# Revit family: Cabinet_Wenger_UltraStor_35
name_source: partatom
category: Furniture
revit_build: Autodesk Revit 2015 (Build: 20140606_1530(x64)
units: mm (PartAtom-declared; Revit-internal decimal feet)

## types (4) — shared parameters
Assembly Code = E2010200
Cabinet Height = 7' - 1 5/8"
Cabinet Panel Thickness = 0' - 0 3/4"
Cabinet Width = 4' - 0 1/2"
Construction Details = http://www.arcat.com
Door Height = 6' - 8 7/8"
Door Width = 1' - 11 1/2"
Green Building-LEED = http://www.arcat.com
Installed Depth = 2' - 5 1/4"
Keynote = 12 35 83
Manufacturer = Wenger Corporation
Manufacturer Fax = (507) 455-4258
Manufacturer Website = https://www.wengercorp.com
Model = #35
Product Data = http://www.arcat.com
Rear Panel Thickness = 0' - 0 3/4"
Revision = R1_2018-04
Sales Information = https://www.wengercorp.com
Specification = http://www.arcat.com
URL = https://www.wengercorp.com
zero-valued in all types: Cost

## per-type parameters (varying)
| type | Description | Door Style | HasDoors | Shelf Thickness |
| UltraStor Cabinet #35 - Comp Grille Doors | Wenger UltraStor Cabinet #35 - Comp Grille Doors | Door_FullHt : Bars | Yes | 0' - 1 1/8" |
| UltraStor Cabinet #35 - Comp Wood Doors | Wenger UltraStor Cabinet #35 - Comp Wood Doors | Door_FullHt : Solid Door | Yes | 0' - 1 1/8" |
| UltraStor Cabinet #35 - Comp Waterfall Grille Doors | Wenger UltraStor Cabinet #35 - Comp Waterfall Grille Doors | Door_FullHt : Waterfall | Yes | 2' - 7 7/32" |
| UltraStor Cabinet #35 - No Doors | Wenger UltraStor Cabinet #35 - No Doors | Door_FullHt : Solid Door | No | 2' - 7 7/32" |

## geometry (parser evidence)
native form markers: Blend x20, Sweep x12
no freeform markers — native parametric forms only
